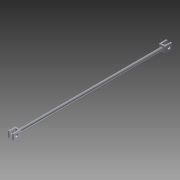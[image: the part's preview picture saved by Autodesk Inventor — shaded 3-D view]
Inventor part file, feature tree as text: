
AUTODESK INVENTOR PART (.ipt)
format: ipt  version: 2012 (Build 160160000, 160)  size: 129,536 bytes
history: native  units: in
note: dims shown in document units (in); Inventor stores cm internally (conversion verified against a paired STEP export)
features: extrude x3, sketch x3, projected_geometry x2, fillet x1
ambient origin geometry x8: Origin, YZ Plane, XZ Plane, XY Plane, X Axis, Y Axis, Z Axis, Center Point
bodies: Solid1 (feature_tree)
feature tree (9):
  extrude  "Extrusion1"  Depth=0.5in
  extrude  "Extrusion2"  Depth=0.625in
  extrude  "Extrusion3"  Depth=0.625in
  fillet  "Fillet1"  Radius=0.5in
  sketch  "Sketch1"  dims[d0=0.5in d1=0.5in]
  sketch  "Sketch2"  dims[d2=13.5in d3=0.0in d4=0.625in]
  sketch  "Sketch3"  dims[d5=0.25in d6=0.625in d7=0.5in d8=0.5in d9=25.0in d10=0.0in d11=0.25in d12=0.25in d13=0.25in d14=0.25in d15=0.125in d16=0.25in d17=0.25in d18=0.25in d19=25.0in d20=0.0in d21=0.125in]
  projected_geometry  "Projected Loop1"
  projected_geometry  "Projected Loop2"
